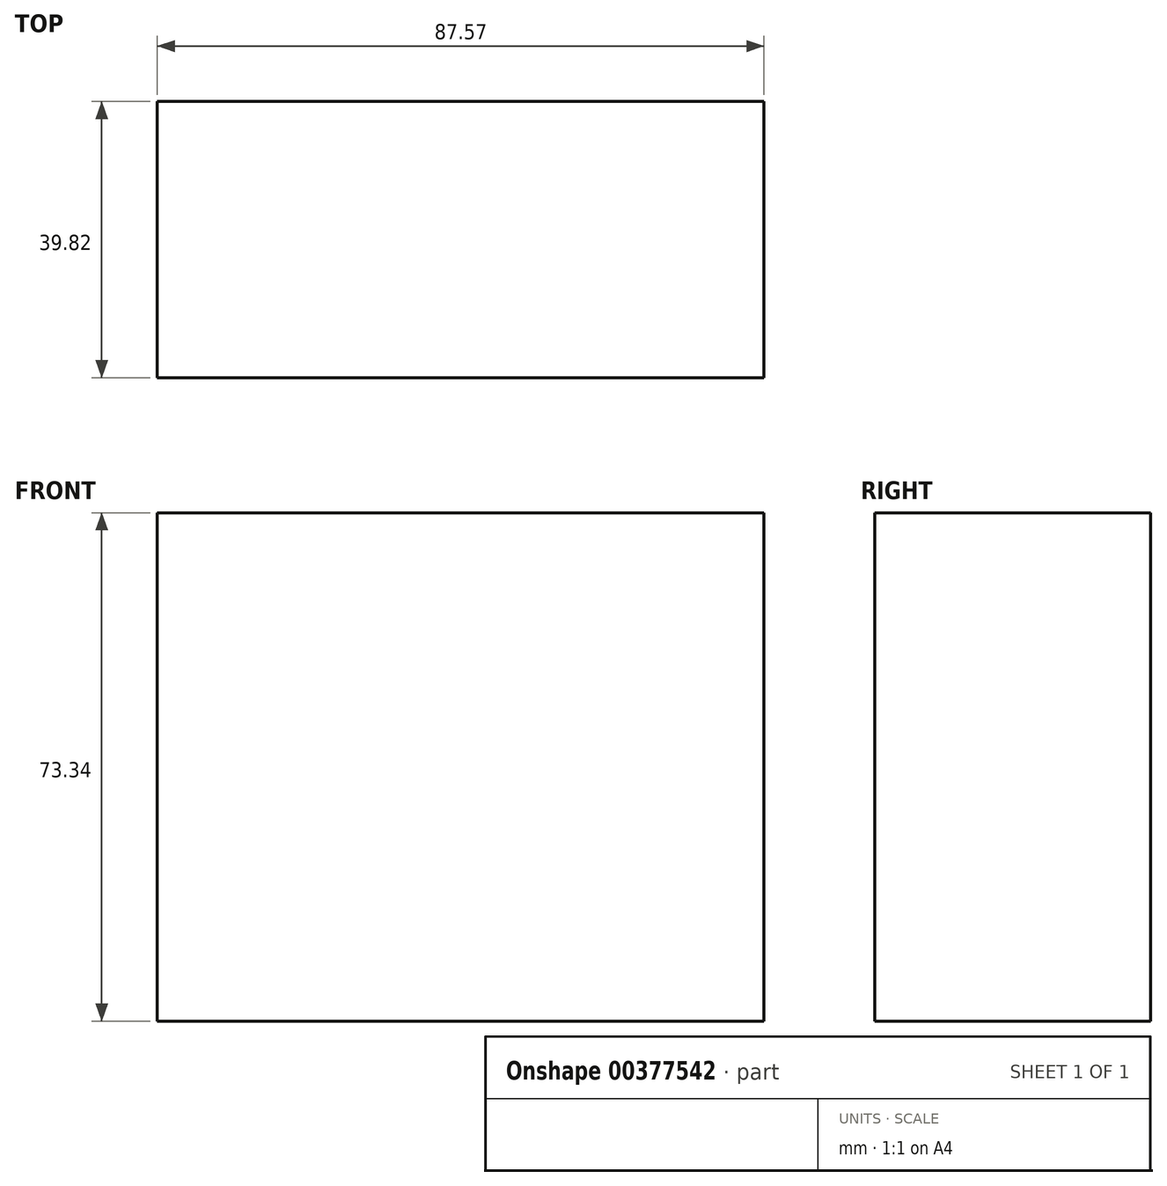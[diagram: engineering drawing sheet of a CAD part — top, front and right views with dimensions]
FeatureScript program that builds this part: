
annotation { "Feature Type Name" : "Feature", "Feature Type Description" : "" }
export const myFeature = defineFeature(function(context is Context, id is Id, definition is map)
    precondition{}
    {
        {
            var Q0;
            Q0=qCreatedBy(makeId("Front.planeOp"),FACE);
            var sketch = newSketch(context, id + "F0", { "sketchPlane" : qUnion([Q0])});
            skLineSegment(sketch, "E0.bottom", {"start": v(48.89, 0) * mm, "end": v(-38.68, 0) * mm});
            skLineSegment(sketch, "E0.top", {"start": v(48.89, 73.34) * mm, "end": v(-38.68, 73.34) * mm});
            skLineSegment(sketch, "E0.left", {"start": v(48.89, 0) * mm, "end": v(48.89, 73.34) * mm});
            skLineSegment(sketch, "E0.right", {"start": v(-38.68, 0) * mm, "end": v(-38.68, 73.34) * mm});
            skSolve(sketch);
        }
        {
            var Q0;
            Q0 = qSketchRegion(id + "F0", true);
            extrude(context, id + "F1", {"entities" : qUnion([Q0]), "depth" : 39.82 * mm});
        }
    });
